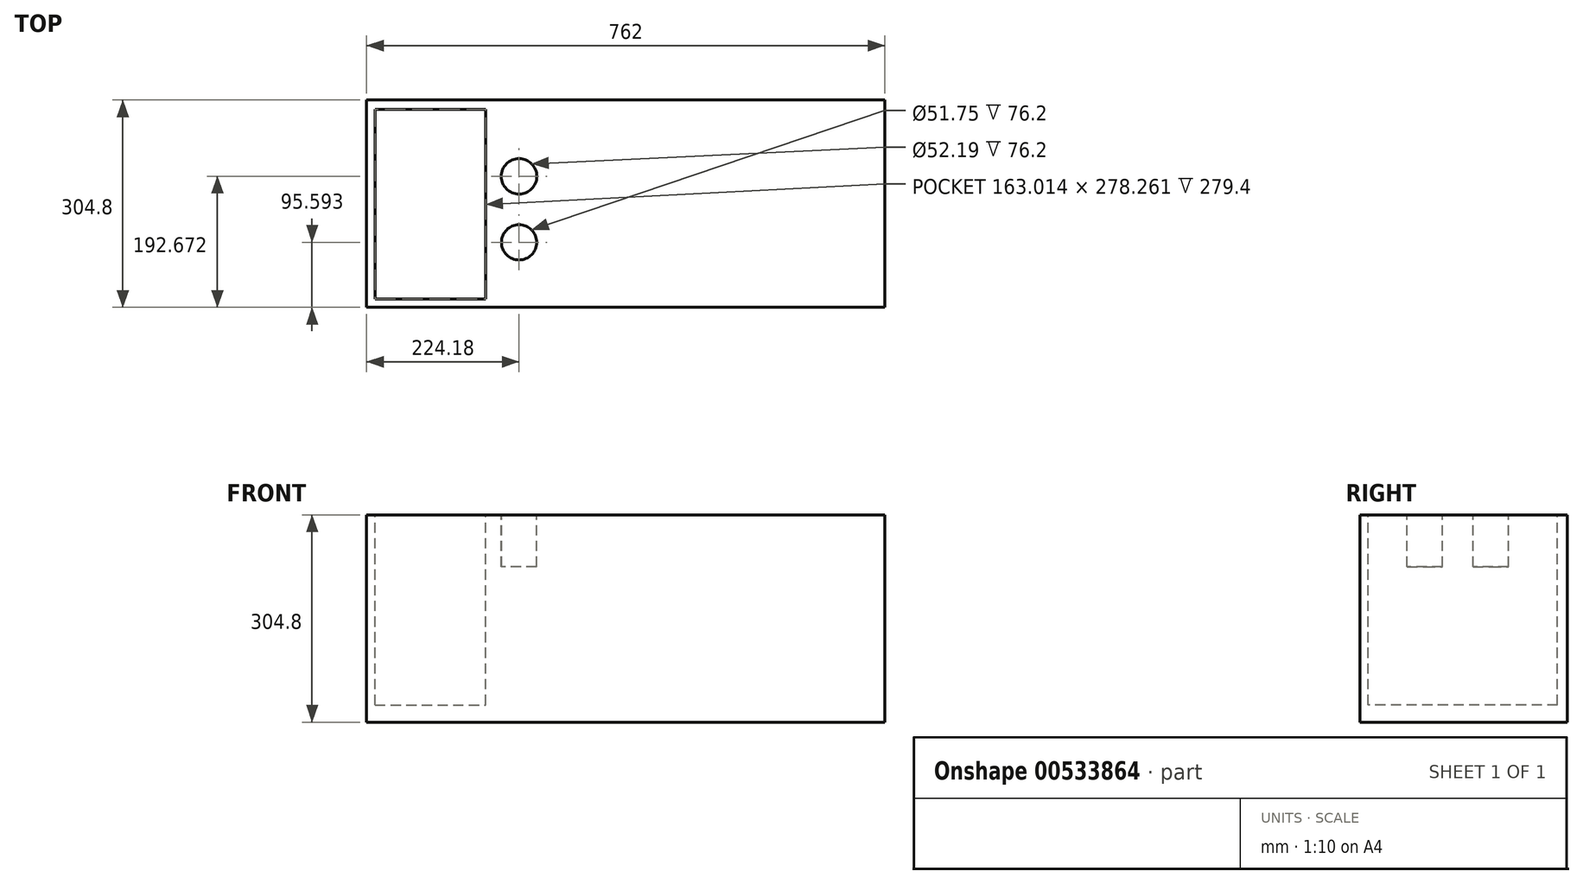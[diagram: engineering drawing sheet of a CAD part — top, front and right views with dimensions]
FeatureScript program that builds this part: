
annotation { "Feature Type Name" : "Feature", "Feature Type Description" : "" }
export const myFeature = defineFeature(function(context is Context, id is Id, definition is map)
    precondition{}
    {
        {
            var Q0;
            Q0=qCreatedBy(makeId("Top.planeOp"),FACE);
            var sketch = newSketch(context, id + "F0", { "sketchPlane" : qUnion([Q0])});
            skLineSegment(sketch, "E0", {"start": v(-382.95, 0) * mm, "end": v(382.95, 0) * mm, "construction": true});
            skPoint(sketch, "E1", {"position": v(0, 0) * mm});
            skLineSegment(sketch, "E2.bottom", {"start": v(-381, 152.4) * mm, "end": v(381, 152.4) * mm});
            skLineSegment(sketch, "E2.top", {"start": v(-381, -152.4) * mm, "end": v(381, -152.4) * mm});
            skLineSegment(sketch, "E2.left", {"start": v(-381, 152.4) * mm, "end": v(-381, -152.4) * mm});
            skLineSegment(sketch, "E2.right", {"start": v(381, 152.4) * mm, "end": v(381, -152.4) * mm});
            skSolve(sketch);
        }
        {
            var Q0;
            Q0 = qSketchRegion(id + "F0", true);
            extrude(context, id + "F1", {"entities" : qUnion([Q0]), "oppositeDirection" : true, "depth" : 304.8 * mm, "offsetDistance" : 25.4 * mm});
        }
        {
            var Q0;
            Q0=makeQuery(id+"F1.opExtrude","CAP_FACE",FACE,{"disambiguationData":[OSD([sQuery(id+"F0.wireOp",EDGE,"E2.bottom"),sQuery(id+"F0.wireOp",EDGE,"E2.top"),sQuery(id+"F0.wireOp",EDGE,"E2.left"),sQuery(id+"F0.wireOp",EDGE,"E2.right")])],"isStart":true});
            var sketch = newSketch(context, id + "F2", { "sketchPlane" : qUnion([Q0])});
            skLineSegment(sketch, "E3.bottom", {"start": v(-368.67, 138.41) * mm, "end": v(-205.66, 138.41) * mm});
            skLineSegment(sketch, "E3.top", {"start": v(-368.67, -139.85) * mm, "end": v(-205.66, -139.85) * mm});
            skLineSegment(sketch, "E3.left", {"start": v(-368.67, 138.41) * mm, "end": v(-368.67, -139.85) * mm});
            skLineSegment(sketch, "E3.right", {"start": v(-205.66, 138.41) * mm, "end": v(-205.66, -139.85) * mm});
            skSolve(sketch);
        }
        {
            var Q0;
            Q0 = qSketchRegion(id + "F2", true);
            extrude(context, id + "F3", {"entities" : qUnion([Q0]), "operationType" : NewBodyOperationType.REMOVE, "oppositeDirection" : true, "depth" : 279.4 * mm, "offsetDistance" : 25.4 * mm});
        }
        {
            var Q0;
            Q0=makeQuery(id+"F1.opExtrude","CAP_FACE",FACE,{"disambiguationData":[OSD([sQuery(id+"F0.wireOp",EDGE,"E2.bottom"),sQuery(id+"F0.wireOp",EDGE,"E2.top"),sQuery(id+"F0.wireOp",EDGE,"E2.left"),sQuery(id+"F0.wireOp",EDGE,"E2.right")])],"isStart":true});
            var sketch = newSketch(context, id + "F4", { "sketchPlane" : qUnion([Q0])});
            skCircle(sketch, "E4", {"center": v(-156.82, 40.27) * mm, "radius": 26.1 * mm});
            skCircle(sketch, "E5", {"center": v(-156.82, -56.8) * mm, "radius": 25.87 * mm});
            skSolve(sketch);
        }
        {
            var Q0;
            Q0 = qSketchRegion(id + "F4", true);
            extrude(context, id + "F5", {"entities" : qUnion([Q0]), "operationType" : NewBodyOperationType.REMOVE, "oppositeDirection" : true, "depth" : 76.2 * mm, "offsetDistance" : 25.4 * mm});
        }
    });
